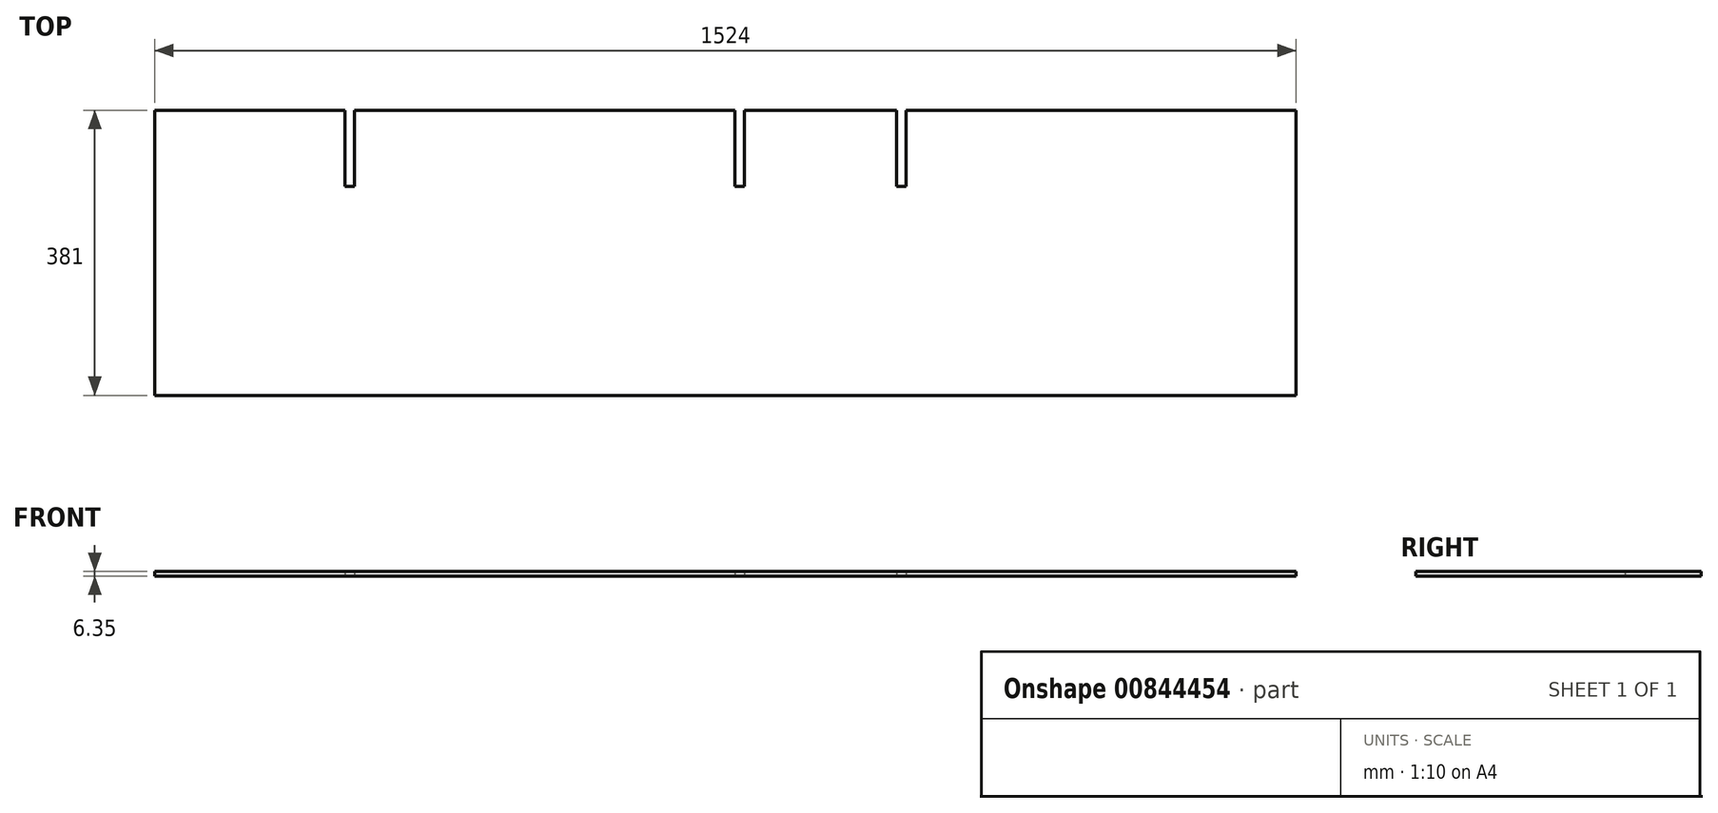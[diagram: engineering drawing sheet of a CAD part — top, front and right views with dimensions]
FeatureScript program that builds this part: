
annotation { "Feature Type Name" : "Feature", "Feature Type Description" : "" }
export const myFeature = defineFeature(function(context is Context, id is Id, definition is map)
    precondition{}
    {
        {
            var Q0;
            Q0=qCreatedBy(makeId("Top.planeOp"),FACE);
            var sketch = newSketch(context, id + "F0", { "sketchPlane" : qUnion([Q0])});
            skLineSegment(sketch, "E0.bottom", {"start": v(-762, 254) * mm, "end": v(762, 254) * mm});
            skLineSegment(sketch, "E0.top", {"start": v(-762, -127) * mm, "end": v(762, -127) * mm});
            skLineSegment(sketch, "E0.left", {"start": v(-762, 254) * mm, "end": v(-762, -127) * mm});
            skLineSegment(sketch, "E0.right", {"start": v(762, 254) * mm, "end": v(762, -127) * mm});
            skLineSegment(sketch, "E1", {"start": v(-508, 254) * mm, "end": v(-508, 152.4) * mm});
            skLineSegment(sketch, "E2", {"start": v(-508, 152.4) * mm, "end": v(-495.3, 152.4) * mm});
            skLineSegment(sketch, "E3", {"start": v(-495.3, 152.4) * mm, "end": v(-495.3, 254) * mm});
            skLineSegment(sketch, "E4", {"start": v(-495.3, 254) * mm, "end": v(-508, 254) * mm});
            skLineSegment(sketch, "E5", {"start": v(12.7, 254) * mm, "end": v(12.7, 152.4) * mm});
            skLineSegment(sketch, "E6", {"start": v(12.7, 152.4) * mm, "end": v(25.4, 152.4) * mm});
            skLineSegment(sketch, "E7", {"start": v(25.4, 152.4) * mm, "end": v(25.4, 254) * mm});
            skLineSegment(sketch, "E8", {"start": v(25.4, 254) * mm, "end": v(12.7, 254) * mm});
            skLineSegment(sketch, "E9", {"start": v(228.6, 254) * mm, "end": v(228.6, 152.4) * mm});
            skLineSegment(sketch, "E10", {"start": v(228.6, 152.4) * mm, "end": v(241.3, 152.4) * mm});
            skLineSegment(sketch, "E11", {"start": v(241.3, 152.4) * mm, "end": v(241.3, 254) * mm});
            skLineSegment(sketch, "E12", {"start": v(241.3, 254) * mm, "end": v(228.6, 254) * mm});
            skSolve(sketch);
        }
        {
            var Q0;
            Q0=makeQuery(id+"F0.imprint","IMPRINT",FACE,{"disambiguationData":[TD([[makeQuery(id+"F0.imprint","IMPRINT",EDGE,{"derivedFrom":sQuery(id+"F0.wireOp",EDGE,"E0.top")}),1.0]])]});
            extrude(context, id + "F1", {"entities" : qUnion([Q0]), "depth" : 6.35 * mm, "offsetDistance" : 25.4 * mm});
        }
    });
